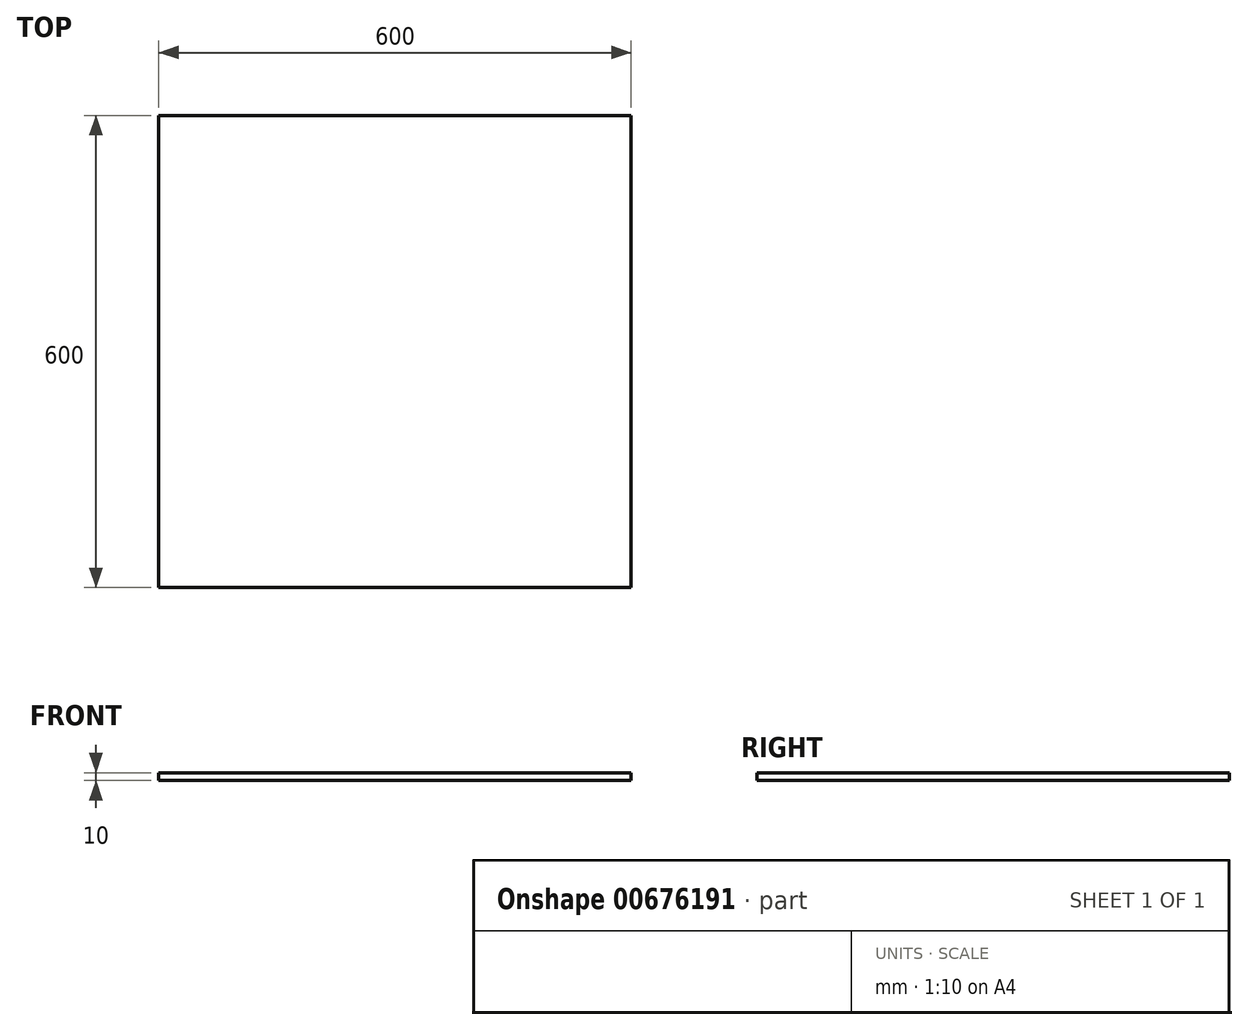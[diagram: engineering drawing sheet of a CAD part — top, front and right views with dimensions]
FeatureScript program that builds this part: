
annotation { "Feature Type Name" : "Feature", "Feature Type Description" : "" }
export const myFeature = defineFeature(function(context is Context, id is Id, definition is map)
    precondition{}
    {
        {
            var Q0;
            Q0=qCreatedBy(makeId("Top.planeOp"),FACE);
            var sketch = newSketch(context, id + "F0", { "sketchPlane" : qUnion([Q0])});
            skLineSegment(sketch, "E0.bottom", {"start": v(300, 300) * mm, "end": v(-300, 300) * mm});
            skLineSegment(sketch, "E0.top", {"start": v(300, -300) * mm, "end": v(-300, -300) * mm});
            skLineSegment(sketch, "E0.left", {"start": v(300, 300) * mm, "end": v(300, -300) * mm});
            skLineSegment(sketch, "E0.right", {"start": v(-300, 300) * mm, "end": v(-300, -300) * mm});
            skPoint(sketch, "E0.middle", {"position": v(0, 0) * mm});
            skSolve(sketch);
        }
        {
            var Q0;
            Q0 = qSketchRegion(id + "F0", true);
            extrude(context, id + "F1", {"entities" : qUnion([Q0]), "depth" : 10 * mm, "offsetDistance" : 25 * mm});
        }
    });
